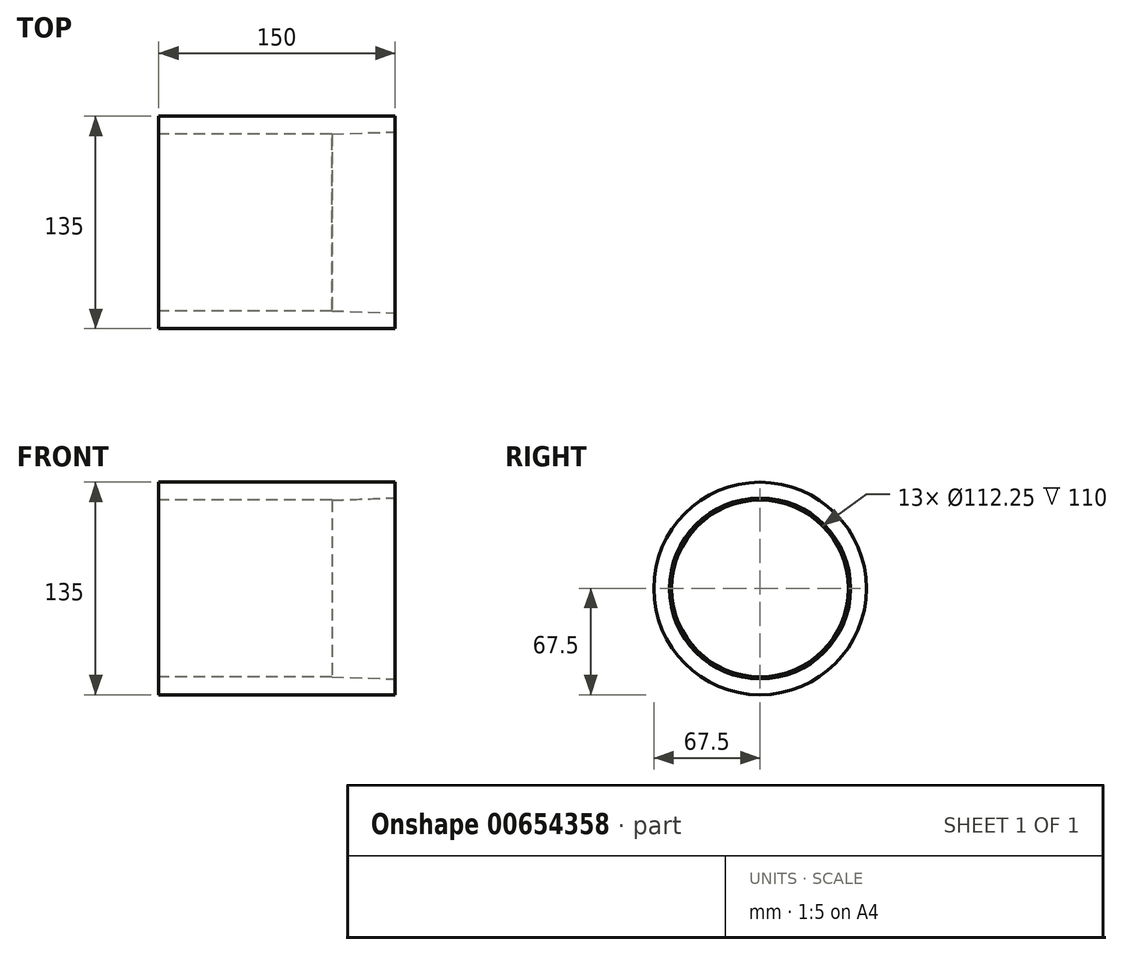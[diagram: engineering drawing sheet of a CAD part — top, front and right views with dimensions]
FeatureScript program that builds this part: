
annotation { "Feature Type Name" : "Feature", "Feature Type Description" : "" }
export const myFeature = defineFeature(function(context is Context, id is Id, definition is map)
    precondition{}
    {
        {
            var Q0;
            Q0=qCreatedBy(makeId("Front.planeOp"),FACE);
            var sketch = newSketch(context, id + "F0", { "sketchPlane" : qUnion([Q0])});
            skLineSegment(sketch, "E0", {"start": v(-75, 0) * mm, "end": v(75, 0) * mm, "construction": true});
            skLineSegment(sketch, "E1.0", {"start": v(-75, 67.5) * mm, "end": v(75, 67.5) * mm});
            skLineSegment(sketch, "E2", {"start": v(0, 114.57) * mm, "end": v(0, -138.79) * mm, "construction": true});
            skLineSegment(sketch, "E3.0", {"start": v(-75, 56.12) * mm, "end": v(35, 56.12) * mm});
            skLineSegment(sketch, "E4", {"start": v(-75, 67.5) * mm, "end": v(-75, 56.12) * mm});
            skLineSegment(sketch, "E5", {"start": v(75, 67.5) * mm, "end": v(75, 57.5) * mm});
            skLineSegment(sketch, "E6.0", {"start": v(35, 67.5) * mm, "end": v(35, 56.12) * mm});
            skLineSegment(sketch, "E7", {"start": v(35, 56.12) * mm, "end": v(75, 57.5) * mm});
            skSolve(sketch);
        }
        {
            var Q0;
            Q0 = qSketchRegion(id + "F0", true);
            var Q1;
            Q1=sQuery(id+"F0.wireOp",EDGE,"E0");
            revolve(context, id + "F1", {"entities" : qUnion([Q0]), "axis" : qUnion([Q1]), "revolveType" : RevolveType.FULL});
        }
    });
